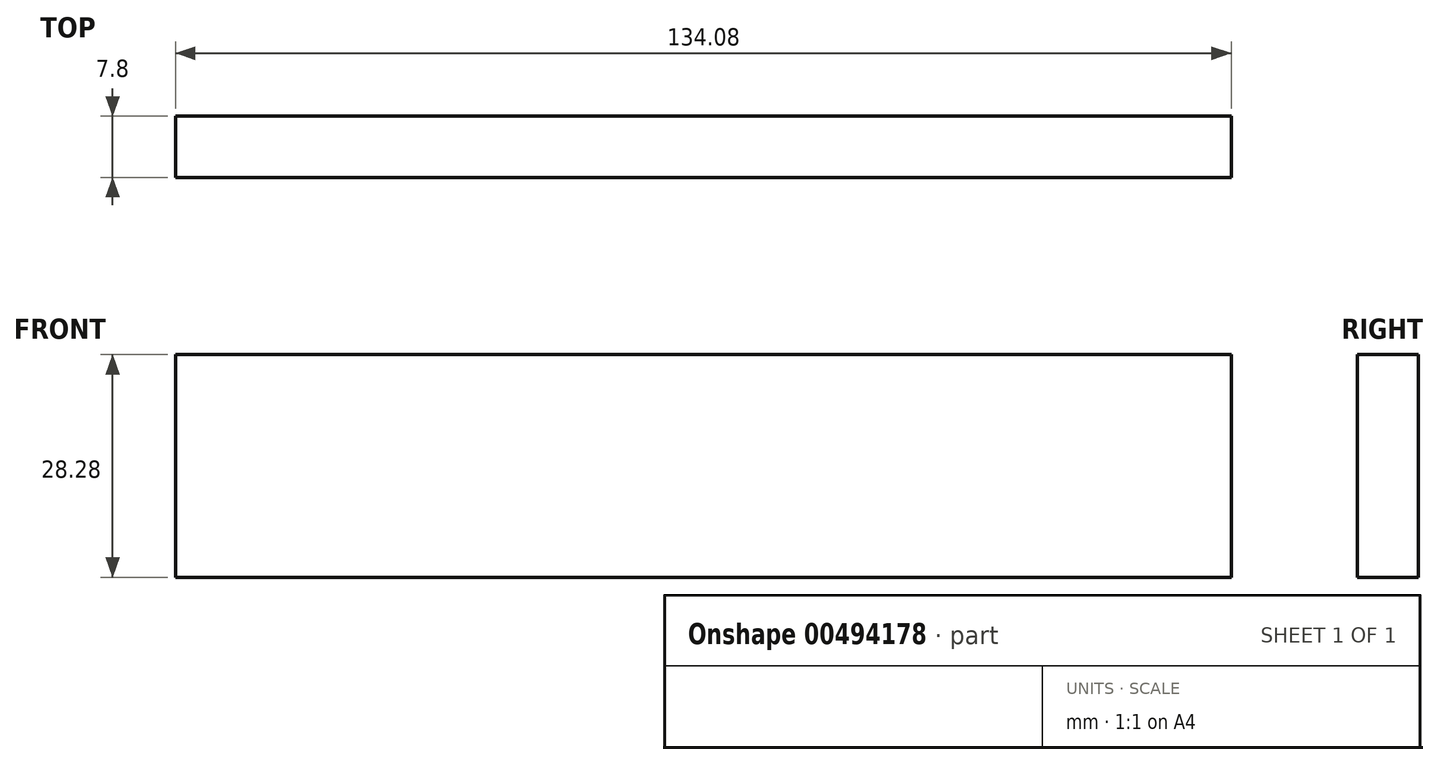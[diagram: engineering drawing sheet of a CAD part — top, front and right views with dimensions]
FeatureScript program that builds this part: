
annotation { "Feature Type Name" : "Feature", "Feature Type Description" : "" }
export const myFeature = defineFeature(function(context is Context, id is Id, definition is map)
    precondition{}
    {
        {
            var Q0;
            Q0=qCreatedBy(makeId("Front.planeOp"),FACE);
            var sketch = newSketch(context, id + "F0", { "sketchPlane" : qUnion([Q0])});
            skLineSegment(sketch, "E0.bottom", {"start": v(67.04, -14.14) * mm, "end": v(-67.04, -14.14) * mm});
            skLineSegment(sketch, "E0.top", {"start": v(67.04, 14.14) * mm, "end": v(-67.04, 14.14) * mm});
            skLineSegment(sketch, "E0.left", {"start": v(67.04, -14.14) * mm, "end": v(67.04, 14.14) * mm});
            skLineSegment(sketch, "E0.right", {"start": v(-67.04, -14.14) * mm, "end": v(-67.04, 14.14) * mm});
            skPoint(sketch, "E0.middle", {"position": v(0, 0) * mm});
            skSolve(sketch);
        }
        {
            var Q0;
            Q0=makeQuery(id+"F0.imprint","IMPRINT",FACE,{"disambiguationData":[TD([[makeQuery(id+"F0.imprint","IMPRINT",EDGE,{"derivedFrom":sQuery(id+"F0.wireOp",EDGE,"E0.bottom")}),-1.0]])]});
            extrude(context, id + "F1", {"entities" : qUnion([Q0]), "endBound" : BoundingType.SYMMETRIC, "depth" : 7.8 * mm});
        }
    });
